# Revit family: Door_SteelWeave_Conceal_FaceOfWallMount_Cookson
name_source: partatom
category: Doors
revit_build: Autodesk Revit Architecture 2016 (Build: 20161004_0715(x64)
units: mm (PartAtom-declared; Revit-internal decimal feet)

## family parameters
Always vertical = Yes
Cut with Voids When Loaded = No
Host = Wall
OmniClass Number = 23.30.10.00
OmniClass Title = Doors
Room Calculation Point = No
Shared = No

## types (6) — shared parameters
A Coil Hood Height = 1' - 5"
Analytic Construction = <None>
Assembly Code = D5020230
B Coil Hood Depth = 1' - 5"
Bottom Bar Material = Stainless Steel
C = 0' - 3"
D = 0' - 3 1/2"
E = 0' - 1 1/2"
Function = Interior
Guide Material = Stainless Steel
Height = 12' - 0"
Manufacturer = Cookson
Manufacturer Fax = 866-448-6798
Model = EAG-10C
Motor = 120V, Single Phase, 60Hz
Operation = Motor Operator
Operator Left Side Horizontal = No
Product Page URL = https://www.cooksondoor.com
Product Specifications URL = https://www.cooksondoor.com
Rough Height = 12' - 0"
URL = http://www.cooksondoor.com
Voltage = 120
Wall Closure = By host
Wall Construction = Steel or Masonry
zero-valued in all types: Weight

## per-type parameters (varying)
| type | Aligned Tube | Description | Door Curtain Mesh | Door Type | Offset Tube | Operator Left Side Top | Operator Right Side Horizontal | Operator Right Side Top | Rough Width | Size Disclaimer | Tube | Width |
| EAG-10C Lago Mesh - Conceal Guides | No | Aesthetic Conceal with Lago Mesh - face of wall mounted guides with tubes. | Door Curtain - Lago Mesh - Cookson | Yes | No | Yes | No | No | 14' - 0" | Lago mesh curtain up to 19' wide by 20' high. | Yes | 14' - 0" |
| EAG-10C Lago Mesh - Conceal Guides wAligned Tube | Yes | Aesthetic Conceal with Lago Mesh - face of wall mounted guides with tubes. | Door Curtain - Lago Mesh - Cookson | Yes | No | No | Yes | No | 14' - 0" | Lago mesh curtain up to 19' wide by 20' high. | Yes | 14' - 0" |
| EAG-10C Tigris Mesh - Conceal Guides | No | Aesthetic Conceal with Tigris Mesh - face of wall mounted guides. | Door Curtain - Tigris Mesh - Cookson | No | No | No | No | Yes | 14' - 0" | Tigris mesh curtain up to 25' wide by 20' high. | No | 14' - 0" |
| EAG-10C Tigris Mesh - Conceal Guides wAligned Tube | Yes | Aesthetic Conceal with Tigris Mesh - face of wall mounted guides with tubes. | Door Curtain - Tigris Mesh - Cookson | No | No | Yes | No | No | 14' - 0" | Tigris mesh curtain up to 25' wide by 20' high. | Yes | 14' - 0" |
| EAG-10C Lago Mesh - Conceal Guides wOffset Tube | No | Aesthetic Conceal with Lago Mesh - face of wall mounted guides with tubes. | Door Curtain - Lago Mesh - Cookson | Yes | Yes | No | Yes | No | 10' - 0" | Lago mesh curtain up to 19' wide by 20' high. | Yes | 10' - 0" |
| EAG-10C Tigris Mesh - Conceal Guides wOffset Tube | No | Aesthetic Conceal with Tigris Mesh - face of wall mounted guides with tubes. | Door Curtain - Tigris Mesh - Cookson | No | Yes | Yes | No | No | 14' - 0" | Tigris mesh curtain up to 25' wide by 20' high. | Yes | 14' - 0" |

note: source unit labels omitted for Voltage — the stored unit's dimension contradicts the parameter name (converter mislabeling)

## geometry (parser evidence)
native form markers: Blend x4, Sweep x6
no freeform markers — native parametric forms only
